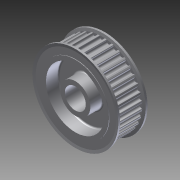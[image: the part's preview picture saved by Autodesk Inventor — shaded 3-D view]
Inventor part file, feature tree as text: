
AUTODESK INVENTOR PART (.ipt)
format: ipt  version: 2014 SP1 (Build 180222100, 222)  size: 1,054,720 bytes
history: native  units: in
note: dims shown in document units (in); Inventor stores cm internally (conversion verified against a paired STEP export)
features: mirror x1, other x1, extrude x1, imported_body x1, sketch x1
ambient origin geometry x8: Origin, YZ Plane, XZ Plane, XY Plane, X Axis, Y Axis, Z Axis, Center Point
bodies: Body1 (feature_tree)
feature tree (5):
  mirror  "Mirror1"
  other  "217-3232-STEP1"
  extrude  "Extrusion1"  [1 undecoded]
  imported_body  "Base1"
  sketch  "Sketch1"  dims[d0=3.937in d1=0.0in]
note: 1 required parameter value undecoded (feature->parameter linkage not recoverable at this tier; creation-order binding heuristic only, values carry confidence <= 0.55)
